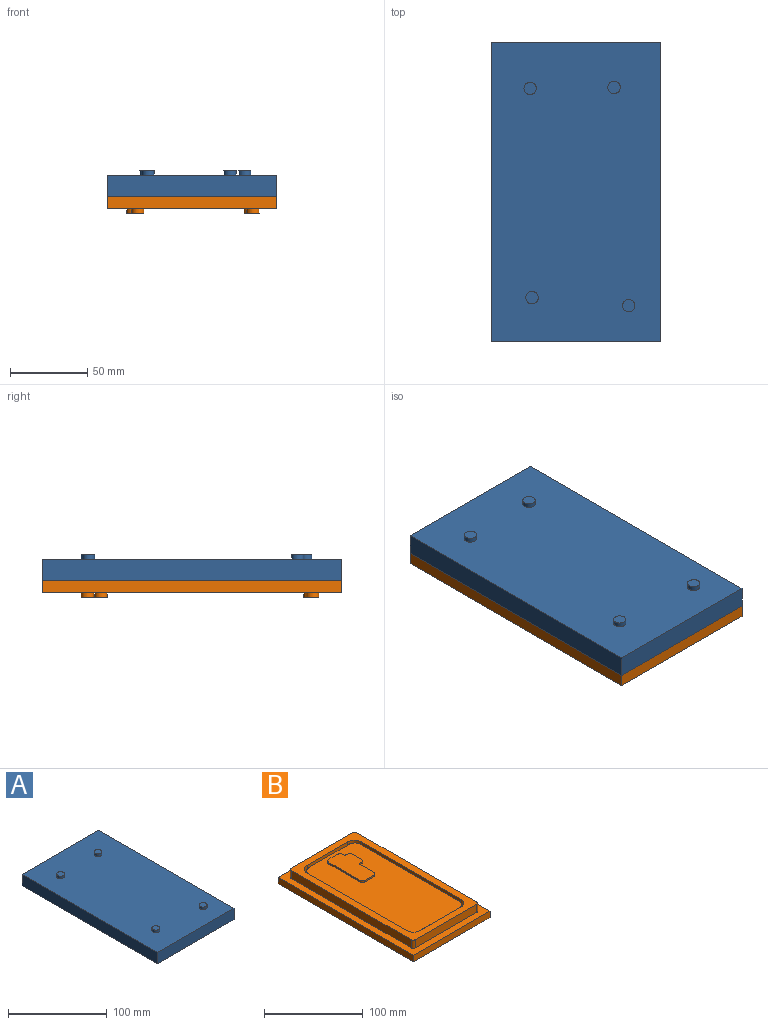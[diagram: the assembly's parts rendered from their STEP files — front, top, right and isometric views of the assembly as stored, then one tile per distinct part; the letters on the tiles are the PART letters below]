
ASSEMBLY  parts=2 mates=1
PART A: 167 faces, bbox 110x194x17 mm
  f0: plane 177x93mm, normal (0,0,-1), area 15546.6mm2, adj f7,f8,f9,f10,f11,f12,f13,f14
  f1: plane 194x110mm, normal (0,0,-1), area 4886.7mm2, adj f2,f3,f4,f5,f7,f8,f9,f10
  f2: plane 110x14mm, normal (0,1,0), area 1540mm2, adj f1,f3,f5,f6
  f3: plane 194x14mm, normal (-1,0,0), area 2716mm2, adj f1,f2,f4,f6
  f4: plane 110x14mm, normal (0,-1,0), area 1540mm2, adj f1,f3,f5,f6
  f5: plane 194x14mm, normal (1,0,0), area 2716mm2, adj f1,f2,f4,f6
  f6: plane 194x110mm, normal (0,0,1), area 21138.9mm2, adj f2,f3,f4,f5,f159,f161,f163,f165
  f7: plane 87x10mm, normal (0,1,0), area 870mm2, adj f0,f1,f11,f14
  f8: plane 171x10mm, normal (1,0,0), area 1710mm2, adj f0,f1,f11,f12
  f9: plane 87x10mm, normal (0,-1,0), area 870mm2, adj f0,f1,f12,f13
  f10: plane 171x10mm, normal (-1,0,0), area 1710mm2, adj f0,f1,f13,f14
  f11: cylinder r=3mm len=10mm, axis (0,0,-1), area 47.1mm2, adj f0,f1,f7,f8
  f12: cylinder r=3mm len=10mm, axis (0,0,1), area 47.1mm2, adj f0,f1,f8,f9
  f13: cylinder r=3mm len=10mm, axis (0,0,-1), area 47.1mm2, adj f0,f1,f9,f10
  f14: cylinder r=3mm len=10mm, axis (0,0,1), area 47.1mm2, adj f0,f1,f7,f10
  f15: extruded ~3x1.74mm, area 6.9mm2, adj f0,f16,f35,f36
  f16: extruded ~3x1.32mm, area 4.1mm2, adj f0,f15,f17,f36
  f17: extruded ~3x1.06mm, area 4.4mm2, adj f0,f16,f18,f36
  f18: extruded ~3x1.93mm, area 6.2mm2, adj f0,f17,f19,f36
  f19: plane 9.16x3mm, normal (-0.31,0.95,0), area 28.9mm2, adj f0,f18,f20,f36
  f20: plane 3.69x3mm, normal (0.87,0.5,0), area 12.8mm2, adj f0,f19,f21,f36
  f21: plane 3x1.92mm, normal (-0.32,0.95,0), area 6.1mm2, adj f0,f20,f22,f36
  f22: plane 3.7x3mm, normal (-0.87,-0.5,0), area 12.8mm2, adj f0,f21,f23,f36
  f23: plane 3.84x3mm, normal (-0.3,0.95,0), area 12.1mm2, adj f0,f22,f24,f36
  f24: plane 3x1.32mm, normal (-0.87,-0.5,0), area 4.6mm2, adj f0,f23,f25,f36
  f25: plane 4.06x3mm, normal (0.02,-1,0), area 12.2mm2, adj f0,f24,f26,f36
  f26: plane 3x2.49mm, normal (-0.6,-0.8,0), area 9.4mm2, adj f0,f25,f27,f36
  f27: plane 3x1.1mm, normal (0.33,-0.95,0), area 3.5mm2, adj f0,f26,f28,f36
  f28: plane 3x2.33mm, normal (0.87,0.5,0), area 8.1mm2, adj f0,f27,f29,f36
  f29: plane 9.12x3mm, normal (0.31,-0.95,0), area 28.8mm2, adj f0,f28,f30,f36
  f30: extruded ~3x2.17mm, area 7.1mm2, adj f0,f29,f31,f36
  f31: extruded ~3x2.28mm, area 9.1mm2, adj f0,f30,f32,f36
  f32: extruded ~3.05x3mm, area 9.6mm2, adj f0,f31,f33,f36
  f33: extruded ~3x1mm, area 3.8mm2, adj f0,f32,f34,f36
  f34: extruded ~3x0.98mm, area 4.1mm2, adj f0,f33,f35,f36
  f35: plane 3x1.74mm, normal (-0.5,0.87,0), area 6mm2, adj f0,f15,f34,f36
  f36: plane 20.43x13.87mm, normal (0,0,-1), area 73.8mm2, adj f15,f16,f17,f18,f19,f20,f21,f22
  f37: plane 9.72x5.59mm, normal (0.87,0.5,0), area 33.6mm2, adj f0,f38,f46,f47
  f38: plane 3x1.89mm, normal (-0.32,0.95,0), area 6mm2, adj f0,f37,f39,f47
  f39: plane 7.18x4.13mm, normal (-0.87,-0.5,0), area 24.8mm2, adj f0,f38,f40,f47
  f40: plane 16.52x3mm, normal (0.16,0.99,0), area 50.2mm2, adj f0,f39,f41,f47
  f41: plane 3x2.12mm, normal (-0.31,0.95,0), area 6.7mm2, adj f0,f40,f42,f47
  f42: plane 8.88x5.11mm, normal (-0.87,-0.5,0), area 30.7mm2, adj f0,f41,f43,f47
  f43: plane 3x1.9mm, normal (0.3,-0.95,0), area 6mm2, adj f0,f42,f44,f47
  f44: plane 6.47x3.73mm, normal (0.87,0.5,0), area 22.4mm2, adj f0,f43,f45,f47
  f45: plane 16.94x3mm, normal (-0.16,-0.99,0), area 51.5mm2, adj f0,f44,f46,f47
  f46: plane 3x1.76mm, normal (0.32,-0.95,0), area 5.6mm2, adj f0,f37,f45,f47
  f47: plane 21.99x14.66mm, normal (0,0,-1), area 80.1mm2, adj f37,f38,f39,f40,f41,f42,f43,f44
  f48: extruded ~3x1.49mm, area 4.6mm2, adj f0,f49,f54,f55
  f49: extruded ~3x0.89mm, area 3.6mm2, adj f0,f48,f50,f55
  f50: extruded ~3x1.08mm, area 3.4mm2, adj f0,f49,f51,f55
  f51: extruded ~3x1.12mm, area 4.2mm2, adj f0,f50,f52,f55
  f52: extruded ~3x1.52mm, area 4.7mm2, adj f0,f51,f53,f55
  f53: extruded ~3x1.89mm, area 6.8mm2, adj f0,f52,f54,f55
  f54: extruded ~3x1.12mm, area 4.4mm2, adj f0,f48,f53,f55
  f55: plane 3.84x3.2mm, normal (0,0,-1), area 8.7mm2, adj f48,f49,f50,f51,f52,f53,f54
  f56: plane 3x2.27mm, normal (0.87,0.5,0), area 7.9mm2, adj f0,f57,f59,f60
  f57: plane 16.64x5.36mm, normal (-0.31,0.95,0), area 52.4mm2, adj f0,f56,f58,f60
  f58: plane 3x2.27mm, normal (-0.87,-0.5,0), area 7.9mm2, adj f0,f57,f59,f60
  f59: plane 16.64x5.36mm, normal (0.31,-0.95,0), area 52.4mm2, adj f0,f56,f58,f60
  f60: plane 17.94x7.63mm, normal (0,0,-1), area 44.8mm2, adj f56,f57,f58,f59
  f61: extruded ~3x1.73mm, area 5.7mm2, adj f0,f62,f75,f76
  f62: extruded ~3x1.37mm, area 5.5mm2, adj f0,f61,f63,f76
  f63: extruded ~3x1.63mm, area 5.5mm2, adj f0,f62,f64,f76
  f64: extruded ~3x2.77mm, area 8.5mm2, adj f0,f63,f65,f76
  f65: plane 3x0.14mm, normal (-0.87,-0.5,0), area 0.5mm2, adj f0,f64,f66,f76
  f66: plane 3x2.91mm, normal (-0.4,0.92,0), area 9.5mm2, adj f0,f65,f67,f76
  f67: plane 3x1.88mm, normal (-0.87,-0.5,0), area 6.5mm2, adj f0,f66,f68,f76
  f68: plane 16.64x5.36mm, normal (0.31,-0.95,0), area 52.4mm2, adj f0,f67,f69,f76
  f69: plane 3x2.27mm, normal (0.87,0.5,0), area 7.9mm2, adj f0,f68,f70,f76
  f70: plane 7.62x3mm, normal (-0.31,0.95,0), area 24mm2, adj f0,f69,f71,f76
  f71: extruded ~3.88x3mm, area 11.8mm2, adj f0,f70,f72,f76
  f72: extruded ~3.33x3mm, area 10.2mm2, adj f0,f71,f73,f76
  f73: extruded ~3x2.14mm, area 8.6mm2, adj f0,f72,f74,f76
  f74: extruded ~3x1.53mm, area 5mm2, adj f0,f73,f75,f76
  f75: plane 3x2.31mm, normal (-0.28,0.96,0), area 7.2mm2, adj f0,f61,f74,f76
  f76: plane 21.22x8.46mm, normal (0,0,-1), area 60.8mm2, adj f61,f62,f63,f64,f65,f66,f67,f68
  f77: extruded ~3x2.75mm, area 10.3mm2, adj f78,f101,f102,f156
  f78: extruded ~3x2.22mm, area 6.9mm2, adj f77,f79,f102,f156
  f79: extruded ~3x1.96mm, area 8.4mm2, adj f78,f80,f102,f156
  f80: extruded ~4.59x3mm, area 14.8mm2, adj f79,f81,f102,f156
  f81: extruded ~4.24x3mm, area 12.8mm2, adj f80,f82,f102,f156
  f82: extruded ~3x2.67mm, area 10.2mm2, adj f81,f83,f102,f156
  f83: extruded ~3x2.46mm, area 7.7mm2, adj f82,f84,f102,f156
  f84: extruded ~3x2.03mm, area 8.3mm2, adj f83,f85,f102,f156
  f85: extruded ~4.49x3mm, area 14.3mm2, adj f84,f101,f102,f156
  f86: extruded ~3x2.6mm, area 8.1mm2, adj f0,f87,f100,f102
  f87: extruded ~3.5x3mm, area 13.9mm2, adj f0,f86,f88,f102
  f88: extruded ~5.3x3mm, area 16.1mm2, adj f0,f87,f89,f102
  f89: extruded ~5.77x3mm, area 18.5mm2, adj f0,f88,f90,f102
  f90: extruded ~3.18x3.05mm, area 13.5mm2, adj f0,f89,f91,f102
  f91: extruded ~3.72x3mm, area 11.6mm2, adj f0,f90,f92,f102
  f92: extruded ~6.03x3.32mm, area 21.4mm2, adj f0,f91,f93,f102
  f93: plane 3x0.11mm, normal (0.87,0.5,0), area 0.4mm2, adj f0,f92,f94,f102
  f94: plane 3.03x3mm, normal (0.39,-0.92,0), area 9.9mm2, adj f0,f93,f95,f102
  f95: plane 3x1.8mm, normal (0.87,0.5,0), area 6.2mm2, adj f0,f94,f96,f102
  f96: plane 16.63x5.38mm, normal (-0.31,0.95,0), area 52.4mm2, adj f0,f95,f97,f102
  f97: plane 3x1.72mm, normal (-0.87,-0.5,0), area 5.9mm2, adj f0,f96,f98,f102
  f98: plane 3x2.84mm, normal (0.15,-0.99,0), area 8.6mm2, adj f0,f97,f99,f102
  f99: plane 3x0.15mm, normal (-0.87,-0.5,0), area 0.5mm2, adj f0,f98,f100,f102
  f100: extruded ~3x2.62mm, area 8.6mm2, adj f0,f86,f99,f102
  f101: extruded ~4.47x3mm, area 13.5mm2, adj f77,f85,f102,f156
  f102: plane 21.52x15.7mm, normal (0,0,-1), area 120mm2, adj f77,f78,f79,f80,f81,f82,f83,f84
  f103: extruded ~3x2.78mm, area 10.4mm2, adj f104,f127,f128,f157
  f104: extruded ~3x1.82mm, area 5.7mm2, adj f103,f105,f128,f157
  f105: extruded ~3x1.18mm, area 4.6mm2, adj f104,f106,f128,f157
  f106: extruded ~3.28x3mm, area 10.5mm2, adj f105,f107,f128,f157
  f107: extruded ~4.26x3.52mm, area 16.7mm2, adj f106,f108,f128,f157
  f108: plane 3x0.16mm, normal (-0.87,-0.5,0), area 0.6mm2, adj f107,f127,f128,f157
  f109: extruded ~4.76x3mm, area 14.9mm2, adj f0,f110,f126,f128
  f110: extruded ~3x2.01mm, area 7.5mm2, adj f0,f109,f111,f128
  f111: extruded ~3x2.12mm, area 8.3mm2, adj f0,f110,f112,f128
  f112: plane 3x1.98mm, normal (-0.5,0.87,0), area 6.8mm2, adj f0,f111,f113,f128
  f113: extruded ~3x2.18mm, area 8.3mm2, adj f0,f112,f114,f128
  f114: extruded ~3x1.61mm, area 6.1mm2, adj f0,f113,f115,f128
  f115: extruded ~3.15x3mm, area 9.9mm2, adj f0,f114,f116,f128
  f116: extruded ~3x2.42mm, area 10.2mm2, adj f0,f115,f117,f128
  f117: plane 3x1.11mm, normal (-0.46,0.89,0), area 3.7mm2, adj f0,f116,f118,f128
  f118: plane 3x0.45mm, normal (0.87,0.5,0), area 1.5mm2, adj f0,f117,f119,f128
  f119: extruded ~5.63x5.08mm, area 23mm2, adj f0,f118,f120,f128
  f120: extruded ~5.11x3mm, area 16.1mm2, adj f0,f119,f121,f128
  f121: extruded ~3x2.49mm, area 9.7mm2, adj f0,f120,f122,f128
  f122: extruded ~3.63x3mm, area 11.4mm2, adj f0,f121,f123,f128
  f123: extruded ~3.4x3mm, area 13.7mm2, adj f0,f122,f124,f128
  f124: extruded ~5.17x3mm, area 15.8mm2, adj f0,f123,f125,f128
  f125: extruded ~5.45x3mm, area 17.3mm2, adj f0,f124,f126,f128
  f126: extruded ~3.77x3.27mm, area 15.4mm2, adj f0,f109,f125,f128
  f127: extruded ~4.61x3mm, area 14mm2, adj f103,f108,f128,f157
  f128: plane 18.78x14.32mm, normal (0,0,-1), area 104.3mm2, adj f103,f104,f105,f106,f107,f108,f109,f110
  f129: plane 3.59x3mm, normal (-0.87,-0.5,0), area 12.4mm2, adj f130,f153,f154,f158
  f130: plane 8.3x3mm, normal (-0.31,0.95,0), area 26.2mm2, adj f129,f131,f154,f158
  f131: plane 3.19x3mm, normal (0.87,0.5,0), area 11mm2, adj f130,f132,f154,f158
  f132: extruded ~3.38x3mm, area 10.6mm2, adj f131,f133,f154,f158
  f133: extruded ~3x2.39mm, area 9.3mm2, adj f132,f134,f154,f158
  f134: extruded ~3.83x3mm, area 12mm2, adj f133,f153,f154,f158
  f135: plane 3.35x3mm, normal (-0.87,-0.5,0), area 11.6mm2, adj f136,f151,f154,f155
  f136: plane 7.27x3mm, normal (-0.31,0.95,0), area 22.9mm2, adj f135,f137,f154,f155
  f137: plane 3x2.85mm, normal (0.87,0.5,0), area 9.9mm2, adj f136,f138,f154,f155
  f138: extruded ~3.23x3mm, area 10.3mm2, adj f137,f139,f154,f155
  f139: extruded ~3x2.11mm, area 8.2mm2, adj f138,f140,f154,f155
  f140: extruded ~3.41x3mm, area 10.7mm2, adj f139,f151,f154,f155
  f141: extruded ~8.45x3mm, area 29.2mm2, adj f0,f142,f152,f154
  f142: plane 5.07x3mm, normal (-0.87,-0.5,0), area 17.5mm2, adj f0,f141,f143,f154
  f143: plane 22.16x7.2mm, normal (0.31,-0.95,0), area 69.9mm2, adj f0,f142,f144,f154
  f144: plane 6.26x3.6mm, normal (0.87,0.5,0), area 21.7mm2, adj f0,f143,f145,f154
  f145: extruded ~4.79x4.56mm, area 20.2mm2, adj f0,f144,f146,f154
  f146: extruded ~5.68x3mm, area 17.8mm2, adj f0,f145,f147,f154
  f147: extruded ~3x2.3mm, area 9.4mm2, adj f0,f146,f148,f154
  f148: extruded ~3.25x3mm, area 9.9mm2, adj f0,f147,f149,f154
  f149: plane 3x0.13mm, normal (-0.5,0.87,0), area 0.5mm2, adj f0,f148,f150,f154
  f150: extruded ~3.61x3mm, area 13.1mm2, adj f0,f149,f152,f154
  f151: extruded ~3x2.92mm, area 12.4mm2, adj f135,f140,f154,f155
  f152: extruded ~3.89x3mm, area 12.1mm2, adj f0,f141,f150,f154
  f153: extruded ~3.25x3.13mm, area 13.8mm2, adj f129,f134,f154,f158
  f154: plane 27.26x18.71mm, normal (0,0,-1), area 169.4mm2, adj f129,f130,f131,f132,f133,f134,f135,f136
  f155: plane 9.99x8.91mm, normal (0,0,-1), area 56.2mm2, adj f135,f136,f137,f138,f139,f140,f151
  f156: plane 14.21x8.55mm, normal (0,0,-1), area 90.7mm2, adj f77,f78,f79,f80,f81,f82,f83,f84
  f157: plane 7.93x5.77mm, normal (0,0,-1), area 28.2mm2, adj f103,f104,f105,f106,f107,f108,f127
  f158: plane 11.14x9.82mm, normal (0,0,-1), area 69.7mm2, adj f129,f130,f131,f132,f133,f134,f153
  f159: cylinder r=4mm len=8mm, axis (0,0,-1), area 75.4mm2, adj f6,f160
  f160: plane 8x8mm, normal (0,0,1), area 50.3mm2, adj f159
  f161: cylinder r=4mm len=8mm, axis (0,0,-1), area 75.4mm2, adj f6,f162
  f162: plane 8x8mm, normal (0,0,1), area 50.3mm2, adj f161
  f163: cylinder r=4mm len=8mm, axis (0,0,-1), area 75.4mm2, adj f6,f164
  f164: plane 8x8mm, normal (0,0,1), area 50.3mm2, adj f163
  f165: cylinder r=4mm len=8mm, axis (0,0,-1), area 75.4mm2, adj f6,f166
  f166: plane 8x8mm, normal (0,0,1), area 50.3mm2, adj f165
PART B: 69 faces, bbox 110x194x21 mm
  f0: plane 99x78mm, normal (0,0,1), area 478.5mm2, adj f3,f4,f5,f10,f11,f12,f22,f23
  f1: plane 78x36mm, normal (0,0,1), area 274.5mm2, adj f3,f5,f6,f10,f12,f13,f24,f25
  f2: plane 158x74mm, normal (0,0,1), area 10470.8mm2, adj f3,f4,f5,f6,f22,f23,f24,f25
  f3: plane 142x8mm, normal (-1,0,0), area 928.4mm2, adj f0,f1,f2,f22,f25,f51,f52,f53
  f4: plane 58x8mm, normal (0,-1,0), area 464mm2, adj f0,f2,f22,f23
  f5: plane 142x8mm, normal (1,0,0), area 1024.4mm2, adj f0,f1,f2,f23,f24,f54,f55,f56
  f6: plane 58x8mm, normal (0,1,0), area 464mm2, adj f1,f2,f24,f25
  f7: plane 88x10mm, normal (0,-1,0), area 880mm2, adj f15,f16,f30,f33
  f8: plane 172x10mm, normal (-1,0,0), area 1720mm2, adj f15,f16,f30,f31
  f9: plane 88x10mm, normal (0,1,0), area 880mm2, adj f15,f16,f31,f32
  f10: plane 142x10mm, normal (1,0,0), area 1212.4mm2, adj f0,f1,f15,f26,f29,f51,f52,f53
  f11: plane 58x10mm, normal (0,1,0), area 580mm2, adj f0,f15,f26,f27
  f12: plane 142x10mm, normal (-1,0,0), area 1308.4mm2, adj f0,f1,f15,f27,f28,f54,f55,f56
  f13: plane 58x10mm, normal (0,-1,0), area 580mm2, adj f1,f15,f28,f29
  f14: plane 172x10mm, normal (1,0,0), area 1720mm2, adj f15,f16,f32,f33
  f15: plane 178x94mm, normal (0,0,1), area 4174.1mm2, adj f7,f8,f9,f10,f11,f12,f13,f14
  f16: plane 194x110mm, normal (0,0,1), area 4615.7mm2, adj f7,f8,f9,f14,f18,f19,f20,f21
  f17: plane 194x110mm, normal (0,0,-1), area 21138.9mm2, adj f18,f19,f20,f21,f61,f63,f65,f67
  f18: plane 110x8mm, normal (0,-1,0), area 880mm2, adj f16,f17,f19,f21
  f19: plane 194x8mm, normal (1,0,0), area 1552mm2, adj f16,f17,f18,f20
  f20: plane 110x8mm, normal (0,1,0), area 880mm2, adj f16,f17,f19,f21
  f21: plane 194x8mm, normal (-1,0,0), area 1552mm2, adj f16,f17,f18,f20
  f22: cylinder r=8mm len=8mm, axis (0,0,1), area 100.5mm2, adj f0,f2,f3,f4
  f23: cylinder r=8mm len=8mm, axis (0,0,-1), area 100.5mm2, adj f0,f2,f4,f5
  f24: cylinder r=8mm len=8mm, axis (0,0,1), area 100.5mm2, adj f1,f2,f5,f6
  f25: cylinder r=8mm len=8mm, axis (0,0,-1), area 100.5mm2, adj f1,f2,f3,f6
  f26: cylinder r=10mm len=10mm, axis (0,0,-1), area 157.1mm2, adj f0,f10,f11,f15
  f27: cylinder r=10mm len=10mm, axis (0,0,1), area 157.1mm2, adj f0,f11,f12,f15
  f28: cylinder r=10mm len=10mm, axis (0,0,-1), area 157.1mm2, adj f1,f12,f13,f15
  f29: cylinder r=10mm len=10mm, axis (0,0,1), area 157.1mm2, adj f1,f10,f13,f15
  f30: cylinder r=3mm len=10mm, axis (0,0,1), area 47.1mm2, adj f7,f8,f15,f16
  f31: cylinder r=3mm len=10mm, axis (0,0,-1), area 47.1mm2, adj f8,f9,f15,f16
  f32: cylinder r=3mm len=10mm, axis (0,0,1), area 47.1mm2, adj f9,f14,f15,f16
  f33: cylinder r=3mm len=10mm, axis (0,0,-1), area 47.1mm2, adj f7,f14,f15,f16
  f34: cylinder r=2mm len=2mm, axis (0,0,-1), area 6.3mm2, adj f2,f35,f49,f50
  f35: plane 2x1mm, normal (1,0,0), area 2mm2, adj f2,f34,f36,f50
  f36: cylinder r=4mm len=4mm, axis (0,0,-1), area 12.6mm2, adj f2,f35,f37,f50
  f37: plane 12x2mm, normal (0,1,0), area 24mm2, adj f2,f36,f38,f50
  f38: cylinder r=4mm len=4mm, axis (0,0,-1), area 12.6mm2, adj f2,f37,f39,f50
  f39: plane 44x2mm, normal (-1,0,0), area 88mm2, adj f2,f38,f40,f50
  f40: cylinder r=4mm len=4mm, axis (0,0,-1), area 12.6mm2, adj f2,f39,f41,f50
  f41: plane 12x2mm, normal (0,-1,0), area 24mm2, adj f2,f40,f42,f50
  f42: cylinder r=4mm len=4mm, axis (0,0,-1), area 12.6mm2, adj f2,f41,f43,f50
  f43: plane 19x2mm, normal (1,0,0), area 38mm2, adj f2,f42,f44,f50
  f44: cylinder r=2mm len=2mm, axis (0,0,-1), area 6.3mm2, adj f2,f43,f45,f50
  f45: plane 3x2mm, normal (0,-1,0), area 6mm2, adj f2,f44,f46,f50
  f46: cylinder r=2mm len=2mm, axis (0,0,-1), area 6.3mm2, adj f2,f45,f47,f50
  f47: plane 16x2mm, normal (1,0,0), area 32mm2, adj f2,f46,f48,f50
  f48: cylinder r=2mm len=2mm, axis (0,0,-1), area 6.3mm2, adj f2,f47,f49,f50
  f49: plane 3x2mm, normal (0,1,0), area 6mm2, adj f2,f34,f48,f50
  f50: plane 52x27mm, normal (0,0,1), area 1166.3mm2, adj f34,f35,f36,f37,f38,f39,f40,f41
  f51: plane 50x2mm, normal (0,0,1), area 100mm2, adj f3,f10,f59,f60
  f52: plane 3x2mm, normal (0,1,0), area 6mm2, adj f1,f3,f10,f60
  f53: plane 3x2mm, normal (0,-1,0), area 6mm2, adj f0,f3,f10,f59
  f54: plane 3x2mm, normal (0,1,0), area 6mm2, adj f1,f5,f12,f57
  f55: plane 3x2mm, normal (0,-1,0), area 6mm2, adj f0,f5,f12,f58
  f56: plane 26x2mm, normal (0,0,1), area 52mm2, adj f5,f12,f57,f58
  f57: cylinder r=1mm len=2mm, axis (1,0,0), area 3.1mm2, adj f5,f12,f54,f56
  f58: cylinder r=1mm len=2mm, axis (-1,0,0), area 3.1mm2, adj f5,f12,f55,f56
  f59: cylinder r=1mm len=2mm, axis (-1,0,0), area 3.1mm2, adj f3,f10,f51,f53
  f60: cylinder r=1mm len=2mm, axis (1,0,0), area 3.1mm2, adj f3,f10,f51,f52
  f61: cylinder r=4mm len=8mm, axis (0,0,1), area 75.4mm2, adj f17,f62
  f62: plane 8x8mm, normal (0,0,-1), area 50.3mm2, adj f61
  f63: cylinder r=4mm len=8mm, axis (0,0,1), area 75.4mm2, adj f17,f64
  f64: plane 8x8mm, normal (0,0,-1), area 50.3mm2, adj f63
  f65: cylinder r=4mm len=8mm, axis (0,0,1), area 75.4mm2, adj f17,f66
  f66: plane 8x8mm, normal (0,0,-1), area 50.3mm2, adj f65
  f67: cylinder r=4mm len=8mm, axis (0,0,1), area 75.4mm2, adj f17,f68
  f68: plane 8x8mm, normal (0,0,-1), area 50.3mm2, adj f67
PLACE A t=(-12.37,-13.05,9.21)mm
PLACE B t=(-12.37,-13.05,9.21)mm
MATE fastened A.f5 <-> B.f19  axis (1,0,0) through (41.74,-110.13,9.21)mm
